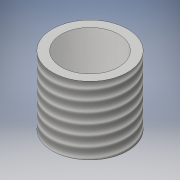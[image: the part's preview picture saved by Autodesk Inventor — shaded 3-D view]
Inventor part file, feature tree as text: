
AUTODESK INVENTOR PART (.ipt)
format: ipt  version: 2019.4 (Build 234330000, 330)  size: 113,664 bytes
history: native  units: in
note: dims shown in document units (in); Inventor stores cm internally (conversion verified against a paired STEP export)
features: extrude x2, sketch x2, thread x1
ambient origin geometry x8: Origin, YZ Plane, XZ Plane, XY Plane, X Axis, Y Axis, Z Axis, Center Point
bodies: Solid1 (feature_tree)
feature tree (5):
  extrude  "Extrusion1"  Depth=0.68in TaperAngle=0.0deg
  extrude  "Extrusion2"  Depth=1.23in TaperAngle=0.0deg
  thread  "Thread1"  [1 undecoded]
  sketch  "Sketch1"  dims[d0=0.75in d1=0.68in d2=0.0in]
  sketch  "Sketch2"  dims[d3=0.57in d4=1.23in d5=0.0in d6=1.0in d7=0.0in]
note: 1 required parameter value undecoded (feature->parameter linkage not recoverable at this tier; creation-order binding heuristic only, values carry confidence <= 0.55)
